# Revit family: NLRS_57_AIR_UN_steel wheather wall louvre bmyt intake LT_sacs
name_source: partatom
category: Air Terminals
revit_build: Autodesk Revit 2018 (Build: 20190510_1515(x64)
units: mm (PartAtom-declared; Revit-internal decimal feet)

## family parameters
Always vertical = No
Cut with Voids When Loaded = Yes
OmniClass Number = 23.75.70.21.27.11
OmniClass Title = Diffusers, Registers, and Grilles
Part Type = Normal
Room Calculation Point = Yes
Round Connector Dimension = Use Diameter
Shared = No
Work Plane-Based = No

## types (2) — shared parameters
Assembly Code = 57.0
Description = Solid Air weather louvre BMY (air intake)
FireRating = 0
IfcDescription = Solid Air weather louvre BMY (air intake)
IfcExportAs = IfcAirTerminal
IfcExportType = LOUVRE
IsExternal = No
LoadBearing = No
LookupTable = BMY
Manufacturer = Solid Air Climate Systems
Max Flow = 0.0 m³/h
Min Flow = 0.0 m³/h
Model = Weather louvre
NLRS_C_content_datum_uitgifte = 01-04-2021
NLRS_C_content_provider = Solid Air Climate Solutions
NLRS_C_content_versie = 3.18.01
NLRS_C_niveau ontwikkeling = LOD 400
SACS_Show_Symbol = No
URL = https://solid-air.nl

## per-type parameters (varying)
| type | SACS_Base_Index | SACS_Factor_NDF1 | SACS_Factor_NDF2 | SACS_Factor_NDF3 | SACS_Factor_NDF4 | SACS_Factor_NDF5 | SACS_Factor_NDF6 |
| BMYTGO | 6 | -3.747714 | -178555.159811 | 4746.924 | -593365.5 | -70673.078935 | 8533288.377894 |
| BMYTSO | 5 | 530601.582661 | -133916.05812 | 3560.193001 | -445024.126692 | -53004.810406 | 6399967.718263 |

## geometry (parser evidence)
native form markers: Sweep x15
no freeform markers — native parametric forms only
